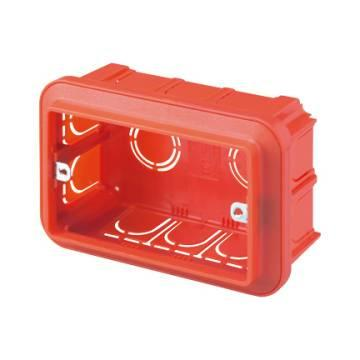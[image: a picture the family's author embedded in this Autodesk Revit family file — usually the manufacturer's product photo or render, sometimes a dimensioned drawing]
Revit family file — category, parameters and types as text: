
# Revit family: Building-ContenitoriIncasso-GEWISS-24SC-SCATOLE-INCASSO_BIGBOX_3P_4P_6P
name_source: partatom
category: Apparecchi elettrici
revit_build: Autodesk Revit 2016 (Build: 20161004_0715(x64)
units: mm (PartAtom-declared; Revit-internal decimal feet)

## family parameters
Condiviso = Sì
Host = Superficie
Mantenere orientamento annotazione = Sì
Numero OmniClass = 23.80.30.14.24
Punto di calcolo locali = Sì
Quota connettore circolare = Usa diametro
Taglio con vuoti quando caricato = Sì
Tipo di parte = Normale
Titolo OmniClass = Junction Boxes

## types (3) — shared parameters
Caratteristiche = Halogen free
Catalogo = BUILDING
Catalogo Serie = 24SC
Centro viti = 182 mm
Codice Electrocod = 0210
Glow Wire Test = 650°C
IDF = 3aa1bd52-a373-4d1b-94b3-c43636d81a1b
IDT = 1294eac5-818f-4a58-8a02-802ca12f5010
Immagine tipo = GW24406.jpg
Incasso = 50 mm  [stored 0.164042 ft]
Installazione = Incasso
Per Pareti = Muratura
Produttore = GEWISS S.p.A.
Prospetto di default = 45 mm
SEO = Scatola
Scheda Tecnica = https://www.gewiss.com
Temperatura di impiego = -15 +60 °C
Termopressione con biglia = 70 °C
Tipo Materiale = Halogen free secondo norma EN 60754-2
Tipo: = Alta capienza
URL = https://www.gewiss.com
Versione file RFA = 19.0

## per-type parameters (varying)
| type | Codice EAN | Descrizione | Descrizione: | Dim. esterne BxHxP (mm) | Interasse fissaggio supporti | Modello | N. moduli SYSTEM | Predisposizione scomparti |
| GW24403 - Scatola 3P | 8011564444522 | SCATOLA 3P.BIGBOX MURATURA | 3 posti | 119x80x50 | 83,5MM | GW24403 | 3 posti | 3 |
| GW24406 - Scatola 6P | 8011564444546 | SCATOLA 6P. BIGBOX MURATURA | 6 posti | 194x90x50 | 100MM | GW24406 | 6 posti | 6 |
| GW24404 - Scatola 4P | 8011564444539 | SCATOLA 4P. BIGBOX MURATURA | 4 posti | 144x85x50 | 108,5MM | GW24404 | 4 posti | 4 |

note: [stored X ft] marks values corroborated as IEEE doubles in the binary element streams (Revit-internal decimal feet)
